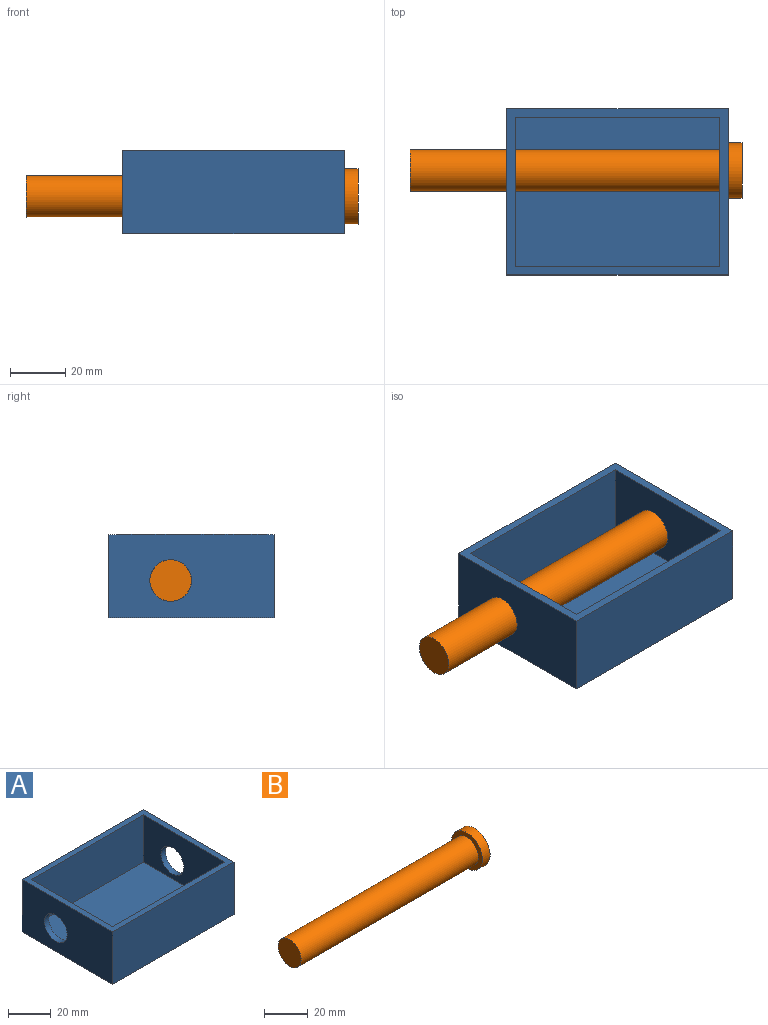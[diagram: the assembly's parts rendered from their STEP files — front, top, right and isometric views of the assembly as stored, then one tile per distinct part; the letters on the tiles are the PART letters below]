
ASSEMBLY  parts=2 mates=1
PART A: 13 faces, bbox 80x60x30 mm
  f0: plane 80x60mm, normal (0,0,1), area 804mm2, adj f1,f2,f3,f4,f6,f7,f8,f9
  f1: plane 60x30mm, normal (1,0,0), area 1623.3mm2, adj f0,f2,f4,f5,f12
  f2: plane 80x30mm, normal (0,1,0), area 2400mm2, adj f0,f1,f3,f5
  f3: plane 60x30mm, normal (-1,0,0), area 1623.3mm2, adj f0,f2,f4,f5,f11
  f4: plane 80x30mm, normal (0,-1,0), area 2400mm2, adj f0,f1,f3,f5
  f5: plane 80x60mm, normal (0,0,-1), area 4800mm2, adj f1,f2,f3,f4
  f6: plane 54x27mm, normal (-1,0,0), area 1281.3mm2, adj f0,f7,f9,f10,f12
  f7: plane 74x27mm, normal (0,-1,0), area 1998mm2, adj f0,f6,f8,f10
  f8: plane 54x27mm, normal (1,0,0), area 1281.3mm2, adj f0,f7,f9,f10,f11
  f9: plane 74x27mm, normal (0,1,0), area 1998mm2, adj f0,f6,f8,f10
  f10: plane 74x54mm, normal (0,0,1), area 3996mm2, adj f6,f7,f8,f9
  f11: cylinder r=7.5mm len=15mm, axis (1,0,0), area 141.4mm2, adj f3,f8
  f12: cylinder r=7.5mm len=15mm, axis (1,0,0), area 141.4mm2, adj f1,f6
PART B: 5 faces, bbox 120x20x20 mm
  f0: cylinder r=7.5mm len=115mm, axis (1,0,0), area 5419.2mm2, adj f1,f3
  f1: plane 15x15mm, normal (-1,0,0), area 176.7mm2, adj f0
  f2: cylinder r=10mm len=20mm, axis (1,0,0), area 314.2mm2, adj f3,f4
  f3: plane 20x20mm, normal (-1,0,0), area 137.4mm2, adj f0,f2
  f4: plane 20x20mm, normal (1,0,0), area 314.2mm2, adj f2
PLACE A at identity fixed
PLACE B rot(axis=(1,0,0),90deg) t=(5,29.65,76.18)mm
MATE slider A.f11 <-> B.f2  axis (1,0,0) through (40,7.73,13.36)mm
